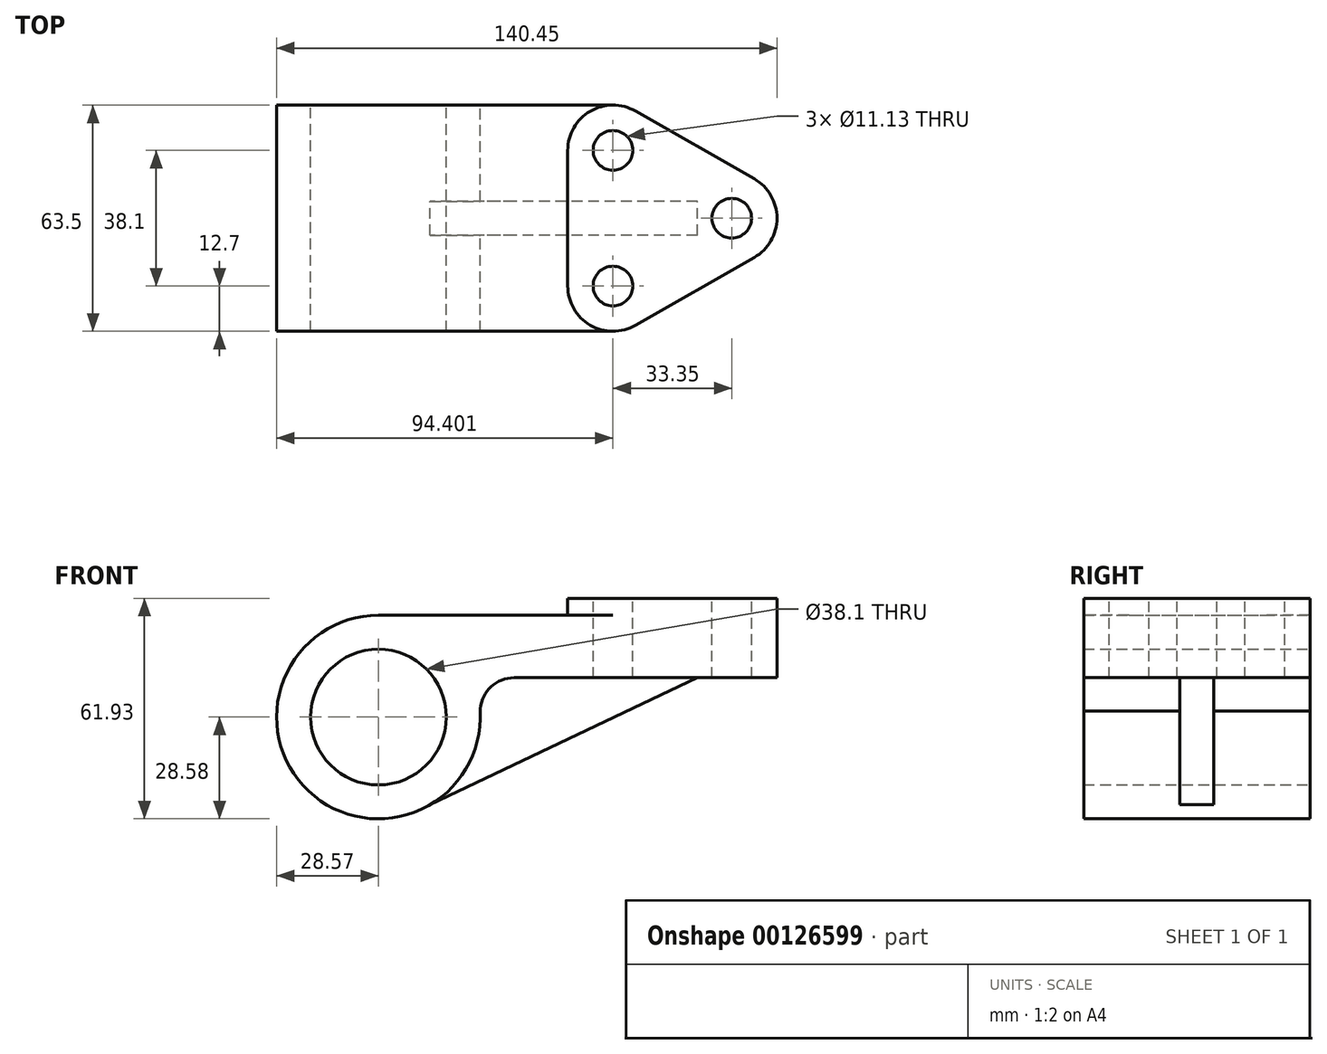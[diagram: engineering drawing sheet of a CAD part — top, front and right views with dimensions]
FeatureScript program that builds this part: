
annotation { "Feature Type Name" : "Feature", "Feature Type Description" : "" }
export const myFeature = defineFeature(function(context is Context, id is Id, definition is map)
    precondition{}
    {
        {
            var Q0;
            Q0=qCreatedBy(makeId("Front.planeOp"),FACE);
            var sketch = newSketch(context, id + "F0", { "sketchPlane" : qUnion([Q0])});
            skLineSegment(sketch, "E0", {"start": v(-41.77, -4.78) * mm, "end": v(70.11, -4.78) * mm});
            skLineSegment(sketch, "E1", {"start": v(70.11, -4.78) * mm, "end": v(70.11, -22.3) * mm});
            skLineSegment(sketch, "E2", {"start": v(47.72, -22.3) * mm, "end": v(-27.28, -57.98) * mm});
            skCircle(sketch, "E3", {"center": v(-41.77, -33.35) * mm, "radius": 19.05 * mm});
            skLineSegment(sketch, "E4", {"start": v(70.11, -22.3) * mm, "end": v(-3.7, -22.3) * mm});
            skArc(sketch, "E5", {"start": v(-13.25, -31.64) * mm, "mid": v(-61.36, -54.15) * mm, "end": v(-41.77, -4.78) * mm});
            skLineSegment(sketch, "E6", {"start": v(-13.25, -31.64) * mm, "end": v(-13.19, -30.99) * mm});
            skPoint(sketch, "E7.visualSharp", {"position": v(-12.42, -22.3) * mm});
            skArc(sketch, "E7.filletArc", {"start": v(-3.7, -22.3) * mm, "mid": v(-10.13, -24.8) * mm, "end": v(-13.19, -30.99) * mm});
            skSolve(sketch);
        }
        {
            var Q0;
            {var subQ5=sQuery(id+"F0.wireOp",EDGE,"E0");Q0=makeQuery(id+"F0.imprint","IMPRINT",FACE,{"disambiguationData":[TD([[makeQuery(id+"F0.imprint","IMPRINT",EDGE,{"derivedFrom":subQ5}),-1.0]])]});}
            extrude(context, id + "F1", {"entities" : qUnion([Q0]), "endBound" : BoundingType.SYMMETRIC, "depth" : 63.5 * mm});
        }
        {
            var Q0;
            {var subQ2=sQuery(id+"F0.wireOp",EDGE,"E2");Q0=makeQuery(id+"F0.imprint","IMPRINT",FACE,{"disambiguationData":[TD([[makeQuery(id+"F0.imprint","IMPRINT",EDGE,{"derivedFrom":subQ2}),-1.0]])]});}
            extrude(context, id + "F2", {"entities" : qUnion([Q0]), "operationType" : NewBodyOperationType.ADD, "endBound" : BoundingType.SYMMETRIC, "depth" : 9.52 * mm});
        }
        {
            var Q0;
            Q0=qCreatedBy(makeId("Top.planeOp"),FACE);
            var sketch = newSketch(context, id + "F3", { "sketchPlane" : qUnion([Q0])});
            skLineSegment(sketch, "E8", {"start": v(11.36, -19.05) * mm, "end": v(11.36, 19.05) * mm});
            skLineSegment(sketch, "E9", {"start": v(30.36, 30.08) * mm, "end": v(63.71, 11.03) * mm});
            skLineSegment(sketch, "E10", {"start": v(63.71, -11.03) * mm, "end": v(30.36, -30.08) * mm});
            skPoint(sketch, "E11.visualSharp", {"position": v(11.36, -40.93) * mm});
            skArc(sketch, "E11.filletArc", {"start": v(11.36, -19.05) * mm, "mid": v(17.69, -30.03) * mm, "end": v(30.36, -30.08) * mm});
            skPoint(sketch, "E12.visualSharp", {"position": v(83.02, 0) * mm});
            skArc(sketch, "E12.filletArc", {"start": v(63.71, -11.03) * mm, "mid": v(70.11, 0) * mm, "end": v(63.71, 11.03) * mm});
            skPoint(sketch, "E13.visualSharp", {"position": v(11.36, 40.93) * mm});
            skArc(sketch, "E13.filletArc", {"start": v(30.36, 30.08) * mm, "mid": v(17.69, 30.03) * mm, "end": v(11.36, 19.05) * mm});
            skCircle(sketch, "E14", {"center": v(24.06, 19.05) * mm, "radius": 5.56 * mm});
            skCircle(sketch, "E15", {"center": v(24.06, -19.05) * mm, "radius": 5.56 * mm});
            skCircle(sketch, "E16", {"center": v(57.41, 0) * mm, "radius": 5.56 * mm});
            skLineSegment(sketch, "E17", {"start": v(24.06, 31.75) * mm, "end": v(70.11, 31.75) * mm});
            skLineSegment(sketch, "E18", {"start": v(70.11, 31.75) * mm, "end": v(70.11, -31.75) * mm});
            skLineSegment(sketch, "E19", {"start": v(70.11, -31.75) * mm, "end": v(24.06, -31.75) * mm});
            skSolve(sketch);
        }
        {
            var Q0;
            {var subQ8=sQuery(id+"F3.wireOp",EDGE,"E8");Q0=makeQuery(id+"F3.imprint","IMPRINT",FACE,{"disambiguationData":[TD([[makeQuery(id+"F3.imprint","IMPRINT",EDGE,{"derivedFrom":subQ8}),-1.0]])]});}
            extrude(context, id + "F4", {"entities" : qUnion([Q0]), "operationType" : NewBodyOperationType.ADD, "oppositeDirection" : true, "depth" : 4.78 * mm});
        }
        {
            var Q0;
            Q0=makeQuery(id+"F3.imprint","IMPRINT",FACE,{"disambiguationData":[TD([[makeQuery(id+"F3.imprint","IMPRINT",EDGE,{"derivedFrom":sQuery(id+"F3.wireOp",EDGE,"E14")}),1.0]])]});
            var Q1;
            Q1=makeQuery(id+"F3.imprint","IMPRINT",FACE,{"disambiguationData":[TD([[makeQuery(id+"F3.imprint","IMPRINT",EDGE,{"derivedFrom":sQuery(id+"F3.wireOp",EDGE,"E16")}),1.0]])]});
            var Q2;
            Q2=makeQuery(id+"F3.imprint","IMPRINT",FACE,{"disambiguationData":[TD([[makeQuery(id+"F3.imprint","IMPRINT",EDGE,{"derivedFrom":sQuery(id+"F3.wireOp",EDGE,"E15")}),1.0]])]});
            extrude(context, id + "F5", {"entities" : qUnion([Q0, Q1, Q2]), "operationType" : NewBodyOperationType.REMOVE, "endBound" : BoundingType.THROUGH_ALL, "oppositeDirection" : true, "depth" : 25.4 * mm});
        }
        {
            var Q0;
            {var subQ4=sQuery(id+"F3.wireOp",EDGE,"E10");Q0=makeQuery(id+"F3.imprint","IMPRINT",FACE,{"disambiguationData":[TD([[makeQuery(id+"F3.imprint","IMPRINT",EDGE,{"derivedFrom":subQ4}),1.0]])]});}
            var Q1;
            {var subQ1=sQuery(id+"F3.wireOp",EDGE,"E9");Q1=makeQuery(id+"F3.imprint","IMPRINT",FACE,{"disambiguationData":[TD([[makeQuery(id+"F3.imprint","IMPRINT",EDGE,{"derivedFrom":subQ1}),1.0]])]});}
            extrude(context, id + "F6", {"entities" : qUnion([Q0, Q1]), "operationType" : NewBodyOperationType.REMOVE, "endBound" : BoundingType.THROUGH_ALL, "oppositeDirection" : true, "depth" : 25.4 * mm});
        }
    });
